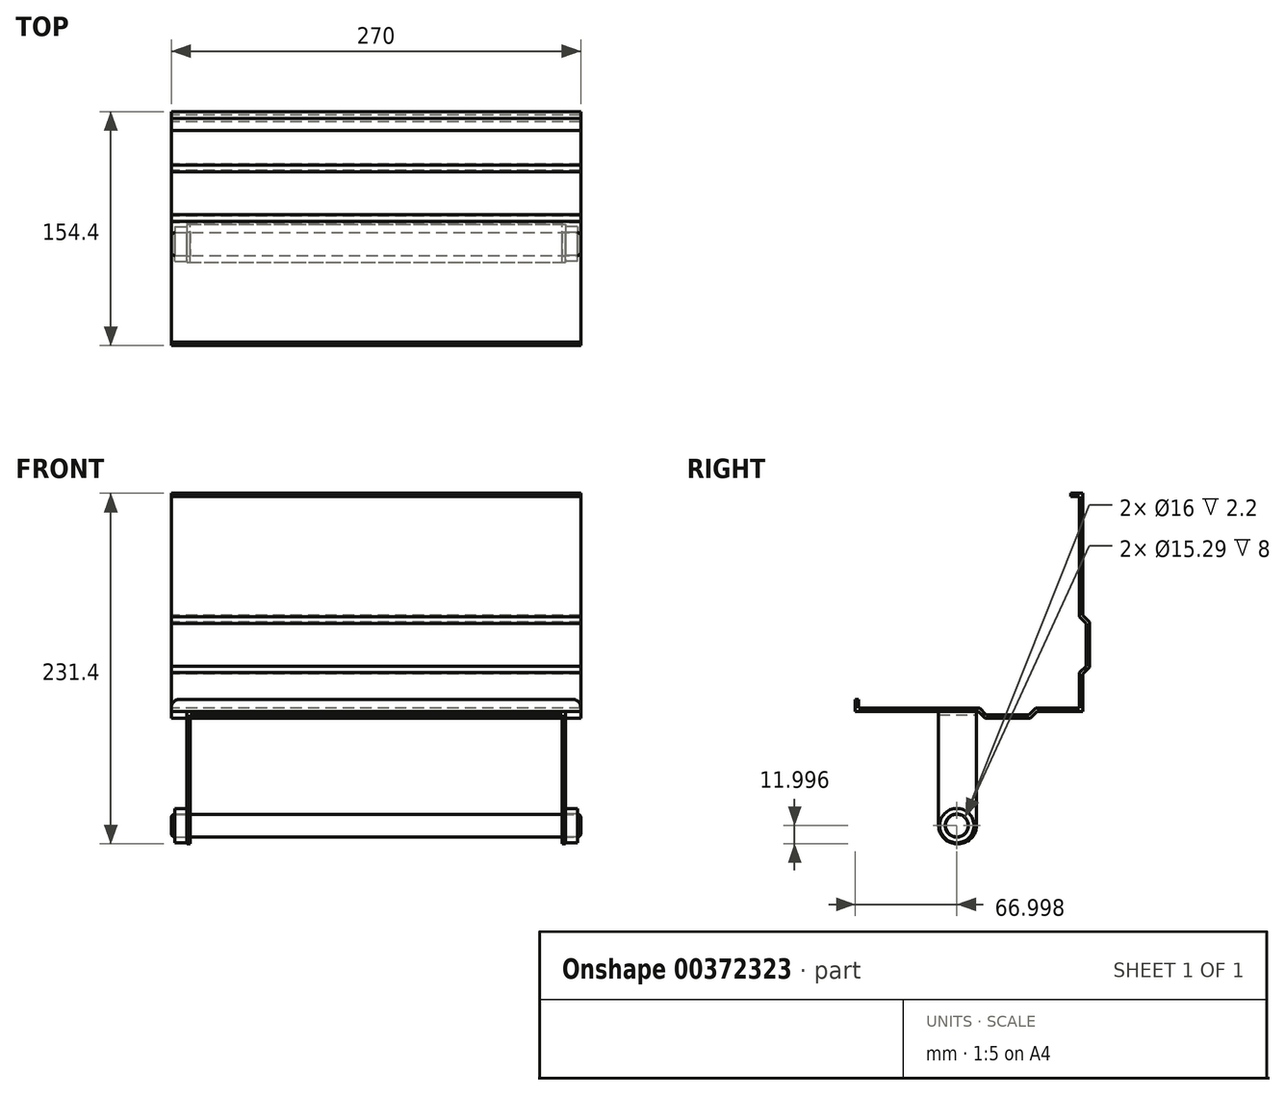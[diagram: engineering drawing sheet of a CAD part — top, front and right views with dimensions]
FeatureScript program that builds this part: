
annotation { "Feature Type Name" : "Feature", "Feature Type Description" : "" }
export const myFeature = defineFeature(function(context is Context, id is Id, definition is map)
    precondition{}
    {
        {
            var Q0;
            Q0=qCreatedBy(makeId("Right.planeOp"),FACE);
            var sketch = newSketch(context, id + "F0", { "sketchPlane" : qUnion([Q0])});
            skLineSegment(sketch, "E0.5", {"start": v(148.32, 120.7) * mm, "end": v(148.32, 90.7) * mm});
            skLineSegment(sketch, "E0.12", {"start": v(146.12, 119.79) * mm, "end": v(146.12, 91.6) * mm});
            skLineSegment(sketch, "E0.18", {"start": v(143.92, 195.7) * mm, "end": v(143.92, 125.1) * mm});
            skLineSegment(sketch, "E1.0", {"start": v(146.12, 91.6) * mm, "end": v(141.72, 87.2) * mm});
            skLineSegment(sketch, "E2.0", {"start": v(148.32, 90.7) * mm, "end": v(143.92, 86.3) * mm});
            skLineSegment(sketch, "E3.0", {"start": v(143.92, 125.1) * mm, "end": v(148.32, 120.7) * mm});
            skLineSegment(sketch, "E4.0", {"start": v(141.72, 124.19) * mm, "end": v(146.12, 119.79) * mm});
            skLineSegment(sketch, "E5.0", {"start": v(135.92, 205.7) * mm, "end": v(135.92, 203.5) * mm});
            skLineSegment(sketch, "E6.right", {"start": v(-6.08, 61.5) * mm, "end": v(-6.08, 63.7) * mm});
            skLineSegment(sketch, "E7.bottom", {"start": v(-6.08, 61.5) * mm, "end": v(-3.88, 61.5) * mm});
            skLineSegment(sketch, "E7.top", {"start": v(-6.08, 69.5) * mm, "end": v(-3.88, 69.5) * mm});
            skLineSegment(sketch, "E7.left", {"start": v(-6.08, 61.5) * mm, "end": v(-6.08, 69.5) * mm});
            skLineSegment(sketch, "E7.right", {"start": v(-3.88, 61.5) * mm, "end": v(-3.88, 69.5) * mm});
            skLineSegment(sketch, "E8.left", {"start": v(141.72, 87.2) * mm, "end": v(141.72, 63.7) * mm});
            skLineSegment(sketch, "E8.right", {"start": v(143.92, 86.3) * mm, "end": v(143.92, 63.7) * mm});
            skLineSegment(sketch, "E9.5", {"start": v(109.4, 57.1) * mm, "end": v(79.4, 57.1) * mm});
            skLineSegment(sketch, "E9.12", {"start": v(108.5, 59.3) * mm, "end": v(80.32, 59.3) * mm});
            skLineSegment(sketch, "E10.0", {"start": v(80.32, 59.3) * mm, "end": v(75.92, 63.7) * mm});
            skLineSegment(sketch, "E11.0", {"start": v(79.4, 57.1) * mm, "end": v(75, 61.5) * mm});
            skLineSegment(sketch, "E12.0", {"start": v(113.8, 61.5) * mm, "end": v(109.4, 57.1) * mm});
            skLineSegment(sketch, "E13.0", {"start": v(112.9, 63.7) * mm, "end": v(108.5, 59.3) * mm});
            skLineSegment(sketch, "E14.trimOffspring", {"start": v(75.92, 63.7) * mm, "end": v(-6.08, 63.7) * mm});
            skLineSegment(sketch, "E15.trimOffspring", {"start": v(75, 61.5) * mm, "end": v(-6.08, 61.5) * mm});
            skLineSegment(sketch, "E16", {"start": v(154.67, 195.7) * mm, "end": v(154.67, 205.7) * mm, "construction": true});
            skLineSegment(sketch, "E17", {"start": v(154.67, 205.7) * mm, "end": v(114.23, 205.7) * mm, "construction": true});
            skLineSegment(sketch, "E18", {"start": v(143.92, 205.7) * mm, "end": v(143.92, 195.7) * mm});
            skLineSegment(sketch, "E19.bottom", {"start": v(135.92, 203.5) * mm, "end": v(143.92, 203.5) * mm});
            skLineSegment(sketch, "E19.top", {"start": v(135.92, 205.7) * mm, "end": v(143.92, 205.7) * mm});
            skLineSegment(sketch, "E19.left", {"start": v(135.92, 203.5) * mm, "end": v(135.92, 205.7) * mm});
            skLineSegment(sketch, "E19.right", {"start": v(143.92, 203.5) * mm, "end": v(143.92, 205.7) * mm});
            skPoint(sketch, "E20.orphan", {"position": v(143.92, 215.7) * mm});
            skLineSegment(sketch, "E21", {"start": v(141.72, 124.19) * mm, "end": v(141.72, 205.7) * mm});
            skLineSegment(sketch, "E22", {"start": v(177.87, 86.3) * mm, "end": v(177.87, 63.7) * mm, "construction": true});
            skLineSegment(sketch, "E23", {"start": v(112.9, 63.7) * mm, "end": v(143.92, 63.7) * mm});
            skLineSegment(sketch, "E24", {"start": v(113.8, 61.5) * mm, "end": v(143.92, 61.5) * mm});
            skLineSegment(sketch, "E25", {"start": v(143.92, 63.7) * mm, "end": v(143.92, 61.5) * mm});
            skSolve(sketch);
        }
        {
            var Q0;
            Q0 = qSketchRegion(id + "F0", true);
            extrude(context, id + "F1", {"entities" : qUnion([Q0]), "depth" : 270 * mm, "offsetDistance" : 25 * mm});
        }
        {
            var Q0;
            Q0=makeQuery(id+"F1.opExtrude","CAP_FACE",FACE,{"disambiguationData":[OSD([sQuery(id+"F0.wireOp",EDGE,"E0.1"),sQuery(id+"F0.wireOp",EDGE,"E0.5"),sQuery(id+"F0.wireOp",EDGE,"E0.12"),sQuery(id+"F0.wireOp",EDGE,"E0.18"),sQuery(id+"F0.wireOp",EDGE,"E1.0"),sQuery(id+"F0.wireOp",EDGE,"E2.0"),sQuery(id+"F0.wireOp",EDGE,"E3.0"),sQuery(id+"F0.wireOp",EDGE,"E4.0"),sQuery(id+"F0.wireOp",EDGE,"E5.0"),sQuery(id+"F0.wireOp",EDGE,"1577aa92-d356-4774-890d-f636edf52f1b.0"),sQuery(id+"F0.wireOp",EDGE,"64eb47f5-7a02-4a22-810b-9f49ee2b35f7.0"),sQuery(id+"F0.wireOp",EDGE,"E6.bottom"),sQuery(id+"F0.wireOp",EDGE,"E6.top"),sQuery(id+"F0.wireOp",EDGE,"E7.bottom"),sQuery(id+"F0.wireOp",EDGE,"E7.top"),sQuery(id+"F0.wireOp",EDGE,"E7.left"),sQuery(id+"F0.wireOp",EDGE,"E7.right"),sQuery(id+"F0.wireOp",EDGE,"E8.top"),sQuery(id+"F0.wireOp",EDGE,"E8.left"),sQuery(id+"F0.wireOp",EDGE,"E8.right")])],"isStart":true});
            cPlane(context, id + "F2", {"entities" : qUnion([Q0]), "cplaneType" : CPlaneType.OFFSET, "offset" : 135 * mm, "oppositeDirection" : true, "width" : 150 * mm, "height" : 150 * mm});
        }
        {
            var Q0;
            Q0=qCreatedBy(id+"F2.planeOp",FACE);
            var sketch = newSketch(context, id + "F3", { "sketchPlane" : qUnion([Q0])});
            skLineSegment(sketch, "E26.bottom", {"start": v(-73.92, 59.3) * mm, "end": v(-48.92, 59.3) * mm});
            skLineSegment(sketch, "E26.top", {"start": v(-73.92, 61.5) * mm, "end": v(-48.92, 61.5) * mm});
            skLineSegment(sketch, "E26.left", {"start": v(-73.92, 59.3) * mm, "end": v(-73.92, 61.5) * mm});
            skLineSegment(sketch, "E26.right", {"start": v(-48.92, 59.3) * mm, "end": v(-48.92, 61.5) * mm});
            skPoint(sketch, "E26.middle", {"position": v(-61.42, 60.4) * mm});
            skSolve(sketch);
        }
        {
            var Q0;
            Q0 = qSketchRegion(id + "F3", true);
            extrude(context, id + "F4", {"entities" : qUnion([Q0]), "depth" : 125 * mm, "offsetDistance" : 25 * mm, "hasSecondDirection" : true, "secondDirectionOppositeDirection" : true, "secondDirectionDepth" : 125 * mm});
        }
        {
            var Q0;
            Q0=makeQuery(id+"F4.opExtrude","SWEPT_FACE",FACE,{"disambiguationData":[OSD([sQuery(id+"F3.wireOp",EDGE,"E26.bottom")])]});
            var sketch = newSketch(context, id + "F5", { "sketchPlane" : qUnion([Q0])});
            skLineSegment(sketch, "E27.bottom", {"start": v(10, -48.92) * mm, "end": v(12.2, -48.92) * mm});
            skLineSegment(sketch, "E27.top", {"start": v(10, -73.92) * mm, "end": v(12.2, -73.92) * mm});
            skLineSegment(sketch, "E27.left", {"start": v(10, -48.92) * mm, "end": v(10, -73.92) * mm});
            skLineSegment(sketch, "E27.right", {"start": v(12.2, -48.92) * mm, "end": v(12.2, -73.92) * mm});
            skLineSegment(sketch, "E28.bottom", {"start": v(260, -48.92) * mm, "end": v(257.8, -48.92) * mm});
            skLineSegment(sketch, "E28.top", {"start": v(260, -73.92) * mm, "end": v(257.8, -73.92) * mm});
            skLineSegment(sketch, "E28.left", {"start": v(260, -48.92) * mm, "end": v(260, -73.92) * mm});
            skLineSegment(sketch, "E28.right", {"start": v(257.8, -48.92) * mm, "end": v(257.8, -73.92) * mm});
            skSolve(sketch);
        }
        {
            var Q0;
            Q0 = qSketchRegion(id + "F5", true);
            extrude(context, id + "F6", {"entities" : qUnion([Q0]), "operationType" : NewBodyOperationType.ADD, "depth" : 85 * mm, "offsetDistance" : 25 * mm});
        }
        {
            var Q0;
            Q0=makeQuery(id+"F6.opExtrude","CAP_EDGE",EDGE,{"disambiguationData":[OSD([sQuery(id+"F5.wireOp",EDGE,"E28.bottom")])],"isStart":false});
            var Q1;
            Q1=makeQuery(id+"F6.opExtrude","CAP_EDGE",EDGE,{"disambiguationData":[OSD([sQuery(id+"F5.wireOp",EDGE,"E28.top")])],"isStart":false});
            var Q2;
            Q2=makeQuery(id+"F6.opExtrude","CAP_EDGE",EDGE,{"disambiguationData":[OSD([sQuery(id+"F5.wireOp",EDGE,"E27.bottom")])],"isStart":false});
            var Q3;
            Q3=makeQuery(id+"F6.opExtrude","CAP_EDGE",EDGE,{"disambiguationData":[OSD([sQuery(id+"F5.wireOp",EDGE,"E27.top")])],"isStart":false});
            fillet(context, id + "F7", {"entities" : qUnion([Q0, Q1, Q2, Q3]), "radius" : 12 * mm, "tangentPropagation" : true, "allowEdgeOverflow" : false});
        }
        {
            var Q0;
            Q0=makeQuery(id+"F6.boolean.opBoolean","MERGE",FACE,{"derivedFrom":[makeQuery(id+"F4.opExtrude","CAP_FACE",FACE,{"disambiguationData":[OSD([sQuery(id+"F3.wireOp",EDGE,"E26.bottom"),sQuery(id+"F3.wireOp",EDGE,"E26.top"),sQuery(id+"F3.wireOp",EDGE,"E26.left"),sQuery(id+"F3.wireOp",EDGE,"E26.right")])],"isStart":true}),makeQuery(id+"F6.opExtrude","SWEPT_FACE",FACE,{"disambiguationData":[OSD([sQuery(id+"F5.wireOp",EDGE,"E28.left")])]})]});
            var sketch = newSketch(context, id + "F8", { "sketchPlane" : qUnion([Q0])});
            skCircle(sketch, "E29", {"center": v(60.92, -13.7) * mm, "radius": 8 * mm});
            skSolve(sketch);
        }
        {
            var Q0;
            Q0 = qSketchRegion(id + "F8", true);
            extrude(context, id + "F9", {"entities" : qUnion([Q0]), "operationType" : NewBodyOperationType.REMOVE, "endBound" : BoundingType.THROUGH_ALL, "oppositeDirection" : true, "depth" : 25 * mm, "offsetDistance" : 25 * mm});
        }
        {
            var Q0;
            Q0=makeQuery(id+"F1.opExtrude","CAP_EDGE",EDGE,{"disambiguationData":[OSD([sQuery(id+"F0.wireOp",EDGE,"E7.top")])],"isStart":false});
            var Q1;
            Q1=makeQuery(id+"F1.opExtrude","CAP_EDGE",EDGE,{"disambiguationData":[OSD([sQuery(id+"F0.wireOp",EDGE,"E7.top")])],"isStart":true});
            fillet(context, id + "F10", {"entities" : qUnion([Q0, Q1]), "radius" : 5 * mm, "tangentPropagation" : true, "allowEdgeOverflow" : false});
        }
        {
            var Q0;
            Q0=qCreatedBy(id+"F2.planeOp",FACE);
            var sketch = newSketch(context, id + "F11", { "sketchPlane" : qUnion([Q0])});
            skCircle(sketch, "E30", {"center": v(-60.92, -13.7) * mm, "radius": 7.5 * mm});
            skSolve(sketch);
        }
        {
            var Q0;
            Q0=makeQuery(id+"F11.imprint","IMPRINT",FACE,{"disambiguationData":[TD([[makeQuery(id+"F11.imprint","IMPRINT",EDGE,{"derivedFrom":sQuery(id+"F11.wireOp",EDGE,"E30")}),1.0]])]});
            var Q1;
            Q1=sQuery(id+"F11.wireOp",EDGE,"E30");
            extrude(context, id + "F12", {"entities" : qUnion([Q0]), "surfaceEntities" : qUnion([Q1]), "depth" : 135 * mm, "offsetDistance" : 25 * mm, "hasSecondDirection" : true, "secondDirectionOppositeDirection" : true, "secondDirectionDepth" : 135 * mm});
        }
        {
            var Q0;
            Q0=makeQuery(id+"F12.opExtrude","CAP_FACE",FACE,{"disambiguationData":[OSD([sQuery(id+"F11.wireOp",EDGE,"E30")])],"isStart":true});
            var Q1;
            Q1=makeQuery(id+"F12.opExtrude","CAP_FACE",FACE,{"disambiguationData":[OSD([sQuery(id+"F11.wireOp",EDGE,"E30")])],"isStart":false});
            fillet(context, id + "F13", {"entities" : qUnion([Q0, Q1]), "radius" : 2 * mm, "tangentPropagation" : true, "allowEdgeOverflow" : false});
        }
        {
            var Q0;
            Q0=makeQuery(id+"F6.boolean.opBoolean","MERGE",FACE,{"derivedFrom":[makeQuery(id+"F4.opExtrude","CAP_FACE",FACE,{"disambiguationData":[OSD([sQuery(id+"F3.wireOp",EDGE,"E26.bottom"),sQuery(id+"F3.wireOp",EDGE,"E26.top"),sQuery(id+"F3.wireOp",EDGE,"E26.left"),sQuery(id+"F3.wireOp",EDGE,"E26.right")])],"isStart":true}),makeQuery(id+"F6.opExtrude","SWEPT_FACE",FACE,{"disambiguationData":[OSD([sQuery(id+"F5.wireOp",EDGE,"E28.left")])]})]});
            var sketch = newSketch(context, id + "F14", { "sketchPlane" : qUnion([Q0])});
            skCircle(sketch, "E31", {"center": v(60.92, -13.7) * mm, "radius": 11.33 * mm});
            skCircle(sketch, "E32", {"center": v(60.92, -13.7) * mm, "radius": 7.64 * mm});
            skSolve(sketch);
        }
        {
            var Q0;
            Q0 = qSketchRegion(id + "F14", true);
            extrude(context, id + "F15", {"entities" : qUnion([Q0]), "depth" : 8 * mm, "offsetDistance" : 25 * mm});
        }
        {
            var Q0;
            Q0=makeQuery(id+"F15.opExtrude","SWEPT_BODY",BODY,{"disambiguationData":[OSD([sQuery(id+"F14.wireOp",EDGE,"E31"),sQuery(id+"F14.wireOp",EDGE,"E32")])]});
            var Q1;
            Q1=qCreatedBy(id+"F2.planeOp",FACE);
            mirror(context, id + "F16", {"operationType" : NewBodyOperationType.ADD, "entities" : qUnion([Q0]), "mirrorPlane" : qUnion([Q1])});
        }
    });
